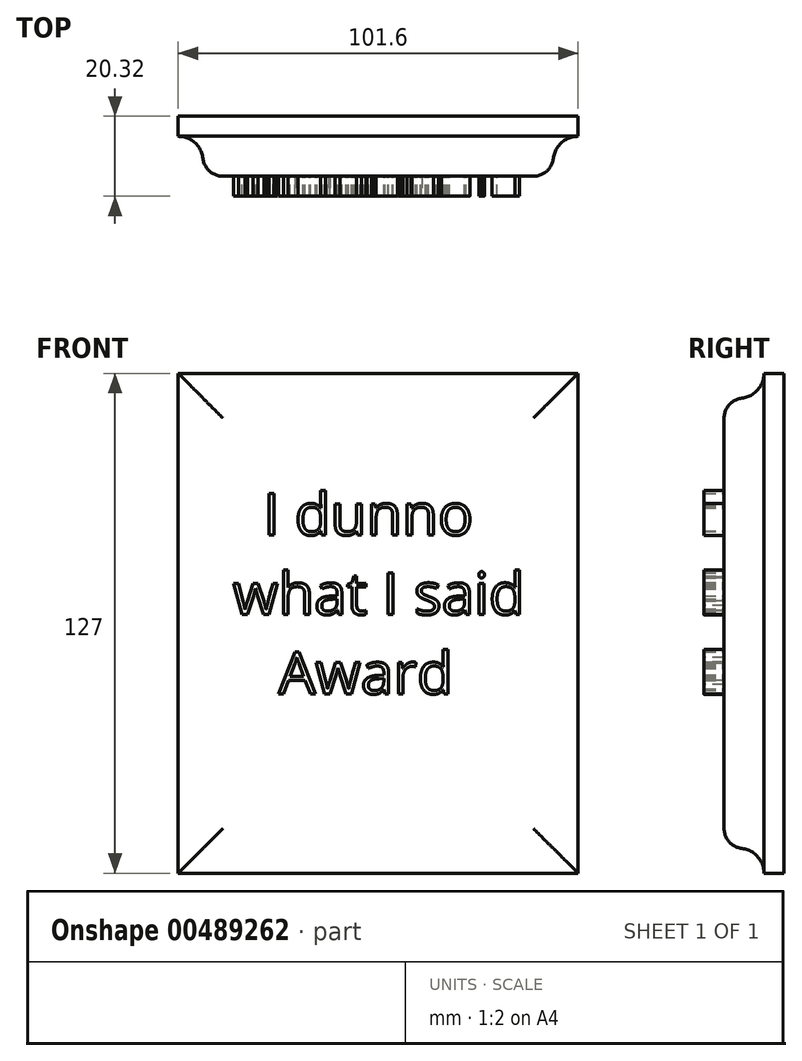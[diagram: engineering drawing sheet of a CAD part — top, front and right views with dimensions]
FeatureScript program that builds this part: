
annotation { "Feature Type Name" : "Feature", "Feature Type Description" : "" }
export const myFeature = defineFeature(function(context is Context, id is Id, definition is map)
    precondition{}
    {
        {
            var Q0;
            Q0=qCreatedBy(makeId("Front.planeOp"),FACE);
            var sketch = newSketch(context, id + "F0", { "sketchPlane" : qUnion([Q0])});
            skLineSegment(sketch, "E0.bottom", {"start": v(-101.6, 127) * mm, "end": v(0, 127) * mm});
            skLineSegment(sketch, "E0.top", {"start": v(-101.6, 0) * mm, "end": v(0, 0) * mm});
            skLineSegment(sketch, "E0.left", {"start": v(-101.6, 127) * mm, "end": v(-101.6, 0) * mm});
            skLineSegment(sketch, "E0.right", {"start": v(0, 127) * mm, "end": v(0, 0) * mm});
            skSolve(sketch);
        }
        {
            var Q0;
            Q0=qSketchRegion(id+"F0",true);
            extrude(context, id + "F1", {"entities" : qUnion([Q0]), "depth" : 15.24 * mm});
        }
        {
            var Q0;
            Q0=makeQuery(id+"F1.opExtrude","CAP_FACE",FACE,{"disambiguationData":[OSD([sQuery(id+"F0.wireOp",EDGE,"E0.bottom"),sQuery(id+"F0.wireOp",EDGE,"E0.top"),sQuery(id+"F0.wireOp",EDGE,"E0.left"),sQuery(id+"F0.wireOp",EDGE,"E0.right")])],"isStart":false});
            var sketch = newSketch(context, id + "F2", { "sketchPlane" : qUnion([Q0])});
            skLineSegment(sketch, "E1.bottom", {"start": v(-6.35, 6.35) * mm, "end": v(-95.25, 6.35) * mm});
            skLineSegment(sketch, "E1.top", {"start": v(-6.35, 120.65) * mm, "end": v(-95.25, 120.65) * mm});
            skLineSegment(sketch, "E1.left", {"start": v(-6.35, 6.35) * mm, "end": v(-6.35, 120.65) * mm});
            skLineSegment(sketch, "E1.right", {"start": v(-95.25, 6.35) * mm, "end": v(-95.25, 120.65) * mm});
            skLineSegment(sketch, "E2.bottom", {"start": v(-101.6, 127) * mm, "end": v(0, 127) * mm});
            skLineSegment(sketch, "E2.top", {"start": v(-101.6, 0) * mm, "end": v(0, 0) * mm});
            skLineSegment(sketch, "E2.left", {"start": v(-101.6, 127) * mm, "end": v(-101.6, 0) * mm});
            skLineSegment(sketch, "E2.right", {"start": v(0, 127) * mm, "end": v(0, 0) * mm});
            skSolve(sketch);
        }
        {
            var Q0;
            Q0=qSketchRegion(id+"F2",true);
            extrude(context, id + "F3", {"entities" : qUnion([Q0]), "operationType" : NewBodyOperationType.REMOVE, "oppositeDirection" : true, "depth" : 10.16 * mm});
        }
        {
            var Q0;
            Q0=makeQuery(id+"F3.boolean.opBoolean","COPY",EDGE,{"derivedFrom":makeQuery(id+"F3.opExtrude","CAP_EDGE",EDGE,{"disambiguationData":[OSD([sQuery(id+"F2.wireOp",EDGE,"E1.top")])],"isStart":false})});
            var Q1;
            Q1=makeQuery(id+"F3.boolean.opBoolean","COPY",EDGE,{"derivedFrom":makeQuery(id+"F3.opExtrude","CAP_EDGE",EDGE,{"disambiguationData":[OSD([sQuery(id+"F2.wireOp",EDGE,"E1.left")])],"isStart":false})});
            var Q2;
            Q2=makeQuery(id+"F3.boolean.opBoolean","COPY",EDGE,{"derivedFrom":makeQuery(id+"F3.opExtrude","CAP_EDGE",EDGE,{"disambiguationData":[OSD([sQuery(id+"F2.wireOp",EDGE,"E1.right")])],"isStart":false})});
            var Q3;
            Q3=makeQuery(id+"F3.boolean.opBoolean","COPY",EDGE,{"derivedFrom":makeQuery(id+"F3.opExtrude","CAP_EDGE",EDGE,{"disambiguationData":[OSD([sQuery(id+"F2.wireOp",EDGE,"E1.bottom")])],"isStart":false})});
            fillet(context, id + "F4", {"entities" : qUnion([Q0, Q1, Q2, Q3]), "radius" : 6.35 * mm, "tangentPropagation" : true, "allowEdgeOverflow" : false});
        }
        {
            var Q0;
            Q0=makeQuery(id+"F1.opExtrude","CAP_FACE",FACE,{"disambiguationData":[OSD([sQuery(id+"F0.wireOp",EDGE,"E0.bottom"),sQuery(id+"F0.wireOp",EDGE,"E0.top"),sQuery(id+"F0.wireOp",EDGE,"E0.left"),sQuery(id+"F0.wireOp",EDGE,"E0.right")])],"isStart":false});
            fillet(context, id + "F5", {"entities" : qUnion([Q0]), "radius" : 5.08 * mm, "tangentPropagation" : true, "allowEdgeOverflow" : false});
        }
        {
            var Q0;
            Q0=makeQuery(id+"F1.opExtrude","CAP_FACE",FACE,{"disambiguationData":[OSD([sQuery(id+"F0.wireOp",EDGE,"E0.bottom"),sQuery(id+"F0.wireOp",EDGE,"E0.top"),sQuery(id+"F0.wireOp",EDGE,"E0.left"),sQuery(id+"F0.wireOp",EDGE,"E0.right")])],"isStart":false});
            var sketch = newSketch(context, id + "F6", { "sketchPlane" : qUnion([Q0])});
            skText(sketch, "E3", { "text": "  I dunno\nwhat I said\n   Award", "fontName": "OpenSans-Regular.ttf"});
            const initialGuessF6  = {"E3": [-0.0877, 0.08591, 1, 0, 0.01068]};
            skSetInitialGuess(sketch, initialGuessF6);
            skSolve(sketch);
        }
        {
            var Q0;
            Q0=qSketchRegion(id+"F6",true);
            extrude(context, id + "F7", {"entities" : qUnion([Q0]), "operationType" : NewBodyOperationType.ADD, "depth" : 5.08 * mm});
        }
    });
